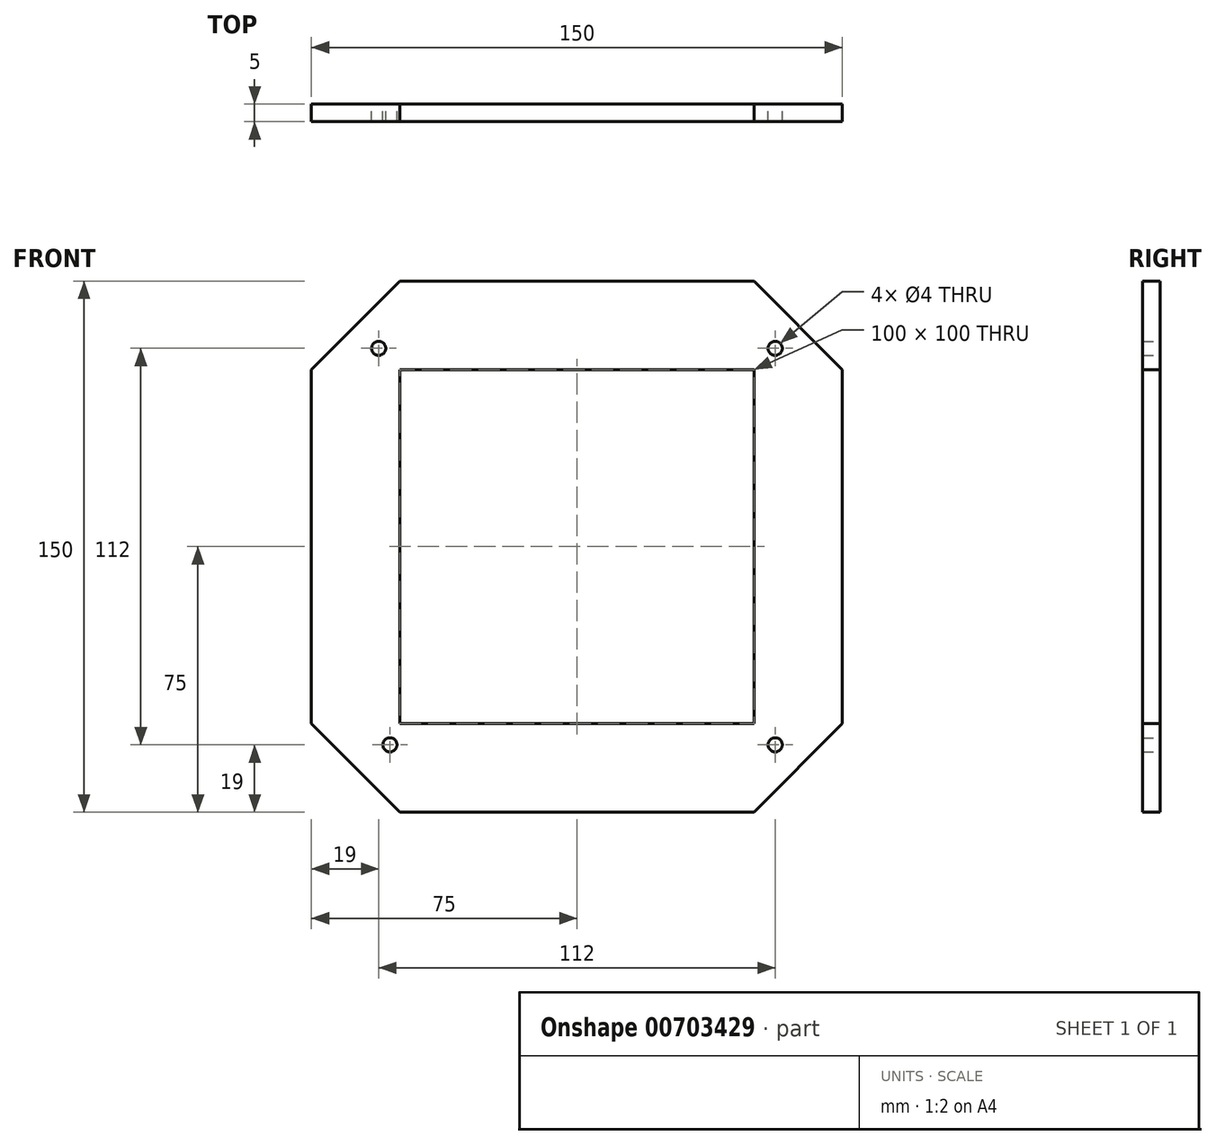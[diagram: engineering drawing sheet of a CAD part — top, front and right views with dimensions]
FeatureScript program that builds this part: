
annotation { "Feature Type Name" : "Feature", "Feature Type Description" : "" }
export const myFeature = defineFeature(function(context is Context, id is Id, definition is map)
    precondition{}
    {
        {
            var Q0;
            Q0=qCreatedBy(makeId("Front.planeOp"),FACE);
            var sketch = newSketch(context, id + "F0", { "sketchPlane" : qUnion([Q0])});
            skLineSegment(sketch, "E0.bottom", {"start": v(75, 75) * mm, "end": v(-75, 75) * mm});
            skLineSegment(sketch, "E0.top", {"start": v(75, -75) * mm, "end": v(-75, -75) * mm});
            skLineSegment(sketch, "E0.left", {"start": v(75, 75) * mm, "end": v(75, -75) * mm});
            skLineSegment(sketch, "E0.right", {"start": v(-75, 75) * mm, "end": v(-75, -75) * mm});
            skPoint(sketch, "E0.middle", {"position": v(0, 0) * mm});
            skLineSegment(sketch, "E1.bottom", {"start": v(50, 50) * mm, "end": v(-50, 50) * mm});
            skLineSegment(sketch, "E1.top", {"start": v(50, -50) * mm, "end": v(-50, -50) * mm});
            skLineSegment(sketch, "E1.left", {"start": v(50, 50) * mm, "end": v(50, -50) * mm});
            skLineSegment(sketch, "E1.right", {"start": v(-50, 50) * mm, "end": v(-50, -50) * mm});
            skSolve(sketch);
        }
        {
            var Q0;
            Q0=makeQuery(id+"F0.imprint","IMPRINT",FACE,{"disambiguationData":[TD([[makeQuery(id+"F0.imprint","IMPRINT",EDGE,{"derivedFrom":sQuery(id+"F0.wireOp",EDGE,"E0.bottom")}),1.0]])]});
            extrude(context, id + "F1", {"entities" : qUnion([Q0]), "depth" : 5 * mm, "offsetDistance" : 25 * mm});
        }
        {
            var Q0;
            Q0=makeQuery(id+"F1.opExtrude","SWEPT_EDGE",EDGE,{"disambiguationData":[OSD([sQuery(id+"F0.wireOp",EDGE,"E0.bottom"),sQuery(id+"F0.wireOp",EDGE,"E0.right")])]});
            var Q1;
            Q1=makeQuery(id+"F1.opExtrude","SWEPT_EDGE",EDGE,{"disambiguationData":[OSD([sQuery(id+"F0.wireOp",EDGE,"E0.bottom"),sQuery(id+"F0.wireOp",EDGE,"E0.left")])]});
            var Q2;
            Q2=makeQuery(id+"F1.opExtrude","SWEPT_EDGE",EDGE,{"disambiguationData":[OSD([sQuery(id+"F0.wireOp",EDGE,"E0.top"),sQuery(id+"F0.wireOp",EDGE,"E0.right")])]});
            var Q3;
            Q3=makeQuery(id+"F1.opExtrude","SWEPT_EDGE",EDGE,{"disambiguationData":[OSD([sQuery(id+"F0.wireOp",EDGE,"E0.top"),sQuery(id+"F0.wireOp",EDGE,"E0.left")])]});
            chamfer(context, id + "F2", {"entities" : qUnion([Q0, Q1, Q2, Q3]), "width" : 25 * mm, "tangentPropagation" : true});
        }
        {
            var Q0;
            Q0=makeQuery(id+"F1.opExtrude","CAP_FACE",FACE,{"disambiguationData":[OSD([sQuery(id+"F0.wireOp",EDGE,"E0.bottom"),sQuery(id+"F0.wireOp",EDGE,"E0.top"),sQuery(id+"F0.wireOp",EDGE,"E0.left"),sQuery(id+"F0.wireOp",EDGE,"E0.right"),sQuery(id+"F0.wireOp",EDGE,"E1.bottom"),sQuery(id+"F0.wireOp",EDGE,"E1.top"),sQuery(id+"F0.wireOp",EDGE,"E1.left"),sQuery(id+"F0.wireOp",EDGE,"E1.right")])],"isStart":false});
            var sketch = newSketch(context, id + "F3", { "sketchPlane" : qUnion([Q0])});
            skCircle(sketch, "E2", {"center": v(-52.82, -56) * mm, "radius": 3.18 * mm});
            skCircle(sketch, "E3", {"center": v(-56, 56) * mm, "radius": 2.76 * mm});
            skCircle(sketch, "E4", {"center": v(56, -56) * mm, "radius": 3.83 * mm});
            skCircle(sketch, "E5", {"center": v(56, 56) * mm, "radius": 3.55 * mm});
            skSolve(sketch);
        }
        {
            var Q0;
            Q0=sQuery(id+"F3.wireOp",VERTEX,"E5.center");
            var Q1;
            Q1=sQuery(id+"F3.wireOp",VERTEX,"E4.center");
            var Q2;
            Q2=sQuery(id+"F3.wireOp",VERTEX,"E2.center");
            var Q3;
            Q3=sQuery(id+"F3.wireOp",VERTEX,"E3.center");
            var Q4;
            Q4=makeQuery(id+"F1.opExtrude","SWEPT_BODY",BODY,{"disambiguationData":[OSD([sQuery(id+"F0.wireOp",EDGE,"E0.bottom"),sQuery(id+"F0.wireOp",EDGE,"E0.top"),sQuery(id+"F0.wireOp",EDGE,"E0.left"),sQuery(id+"F0.wireOp",EDGE,"E0.right"),sQuery(id+"F0.wireOp",EDGE,"E1.bottom"),sQuery(id+"F0.wireOp",EDGE,"E1.top"),sQuery(id+"F0.wireOp",EDGE,"E1.left"),sQuery(id+"F0.wireOp",EDGE,"E1.right")])]});
            hole(context, id + "F4", {"style" : HoleStyle.SIMPLE, "endStyle" : HoleEndStyle.THROUGH, "holeDiameter" : 4 * mm, "majorDiameter" : 5 * mm, "isTappedThrough" : true, "tappedDepth" : 12 * mm, "tapClearance" : 3, "locations" : qUnion([Q0, Q1, Q2, Q3]), "scope" : qUnion([Q4]), "startStyle" : HoleStartStyle.PART});
        }
    });
